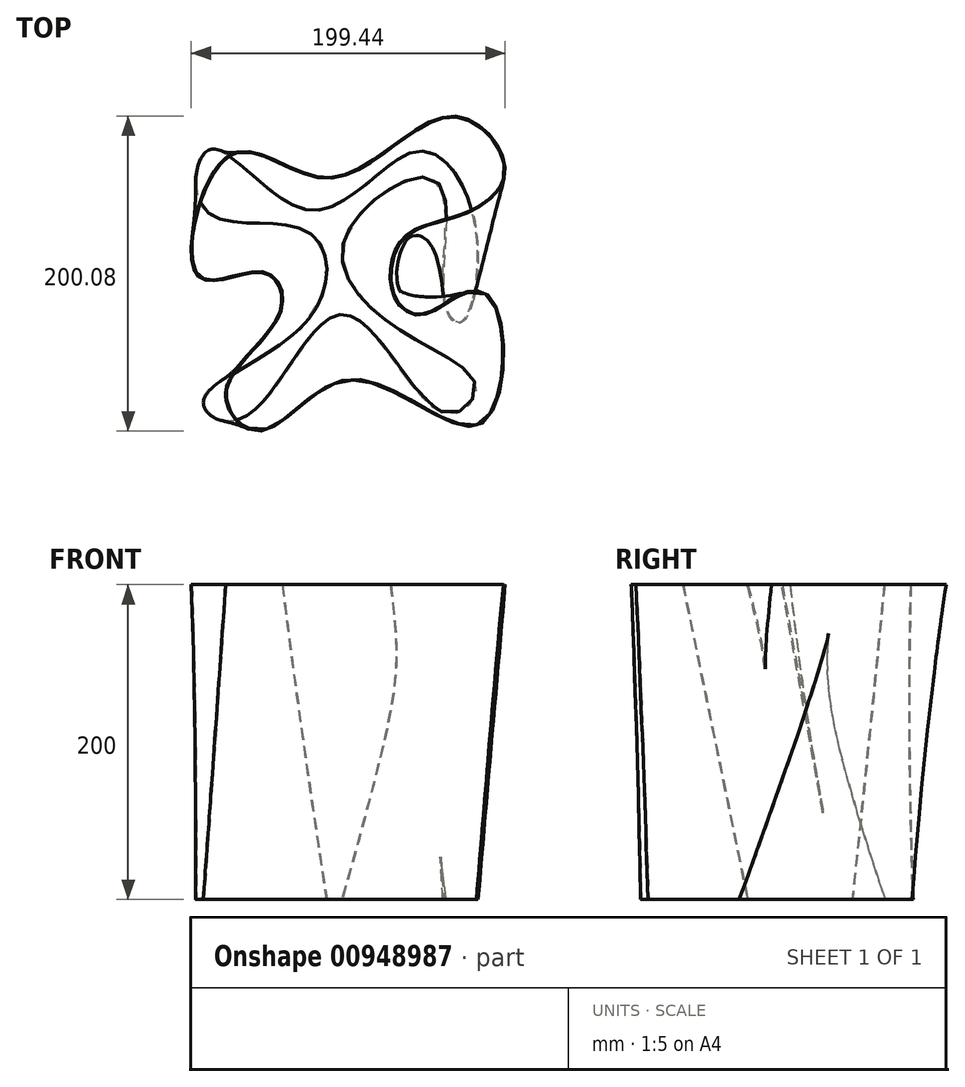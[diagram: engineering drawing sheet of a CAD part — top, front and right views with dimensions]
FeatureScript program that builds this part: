
annotation { "Feature Type Name" : "Feature", "Feature Type Description" : "" }
export const myFeature = defineFeature(function(context is Context, id is Id, definition is map)
    precondition{}
    {
        {
            var Q0;
            Q0=qCreatedBy(makeId("Top.planeOp"),FACE);
            var sketch = newSketch(context, id + "F0", { "sketchPlane" : qUnion([Q0])});
            skLineSegment(sketch, "E0.bottom", {"start": v(-106.47, -103.23) * mm, "end": v(93.53, -103.23) * mm, "construction": true});
            skLineSegment(sketch, "E0.top", {"start": v(-106.47, 96.77) * mm, "end": v(93.53, 96.77) * mm, "construction": true});
            skLineSegment(sketch, "E0.left", {"start": v(-106.47, -103.23) * mm, "end": v(-106.47, 96.77) * mm, "construction": true});
            skLineSegment(sketch, "E0.right", {"start": v(93.53, -103.23) * mm, "end": v(93.53, 96.77) * mm, "construction": true});
            skFitSpline(sketch, "E1", {"points": [v(-92.1, -78.03) * mm, v(-25.95, -25.91) * mm, v(-26, 29.38) * mm, v(-91.31, 43.19) * mm, v(-87.45, 82) * mm, v(-24.2, 43.89) * mm, v(42.86, 81.24) * mm, v(80.39, 36.22) * mm, v(71.8, -27.83) * mm, v(60.52, -13.05) * mm, v(54.7, 62.42) * mm, v(-2, 25.05) * mm, v(34.1, -33.1) * mm, v(81.3, -68.93) * mm, v(60.58, -85.54) * mm, v(-3.4, -23.2) * mm, v(-67.38, -89.15) * mm, v(-92.1, -78.03) * mm]});
            skSolve(sketch);
        }
        {
            var Q0;
            Q0=qCreatedBy(makeId("Top.planeOp"),FACE);
            cPlane(context, id + "F1", {"entities" : qUnion([Q0]), "cplaneType" : CPlaneType.OFFSET, "offset" : 200 * mm, "width" : 150 * mm, "height" : 150 * mm});
        }
        {
            var Q0;
            Q0=qCreatedBy(id+"F1.planeOp",FACE);
            var sketch = newSketch(context, id + "F2", { "sketchPlane" : qUnion([Q0])});
            skLineSegment(sketch, "E2.bottom", {"start": v(-100.35, -96.83) * mm, "end": v(99.65, -96.83) * mm, "construction": true});
            skLineSegment(sketch, "E2.top", {"start": v(-100.35, 103.17) * mm, "end": v(99.65, 103.17) * mm, "construction": true});
            skLineSegment(sketch, "E2.left", {"start": v(-100.35, -96.83) * mm, "end": v(-100.35, 103.17) * mm, "construction": true});
            skLineSegment(sketch, "E2.right", {"start": v(99.65, -96.83) * mm, "end": v(99.65, 103.17) * mm, "construction": true});
            skFitSpline(sketch, "E3", {"points": [v(-77.8, -71.84) * mm, v(-43.95, -22.24) * mm, v(-53.88, 3.63) * mm, v(-95.45, 1.69) * mm, v(-74.76, 78.64) * mm, v(-11.54, 64.12) * mm, v(65.32, 103.17) * mm, v(99.65, 69.02) * mm, v(72.43, 40.45) * mm, v(34.44, 24.5) * mm, v(29.51, -11.37) * mm, v(46.34, -22.67) * mm, v(69.88, -10.65) * mm, v(91.96, -14.35) * mm, v(83.83, -92.42) * mm, v(2.69, -64.35) * mm, v(-55.63, -96.83) * mm, v(-77.8, -71.84) * mm]});
            skSolve(sketch);
        }
        {
            var Q0;
            Q0=makeQuery(id+"F0.imprint","IMPRINT",FACE,{"disambiguationData":[TD([[makeQuery(id+"F0.imprint","IMPRINT",EDGE,{"derivedFrom":sQuery(id+"F0.wireOp",EDGE,"E1")}),-1.0]])]});
            var Q1;
            Q1=makeQuery(id+"F2.imprint","IMPRINT",FACE,{"disambiguationData":[TD([[makeQuery(id+"F2.imprint","IMPRINT",EDGE,{"derivedFrom":sQuery(id+"F2.wireOp",EDGE,"E3")}),-1.0]])]});
            loft(context, id + "F3", {"sheetProfilesArray" : [{ "sheetProfileEntities" : qUnion([Q0]) }, { "sheetProfileEntities" : qUnion([Q1]) }]});
        }
        {
            var Q0;
            Q0=makeQuery(id+"F3.opLoft","CAP_FACE",FACE,{"disambiguationData":[OSD([makeQuery(id+"F2.imprint","IMPRINT",FACE,{"disambiguationData":[TD([[makeQuery(id+"F2.imprint","IMPRINT",EDGE,{"derivedFrom":sQuery(id+"F2.wireOp",EDGE,"E3")}),-1.0]])]})])],"isStart":true});
            shell(context, id + "F4", {"entities" : qUnion([Q0]), "thickness" : .5 * mm});
        }
    });
